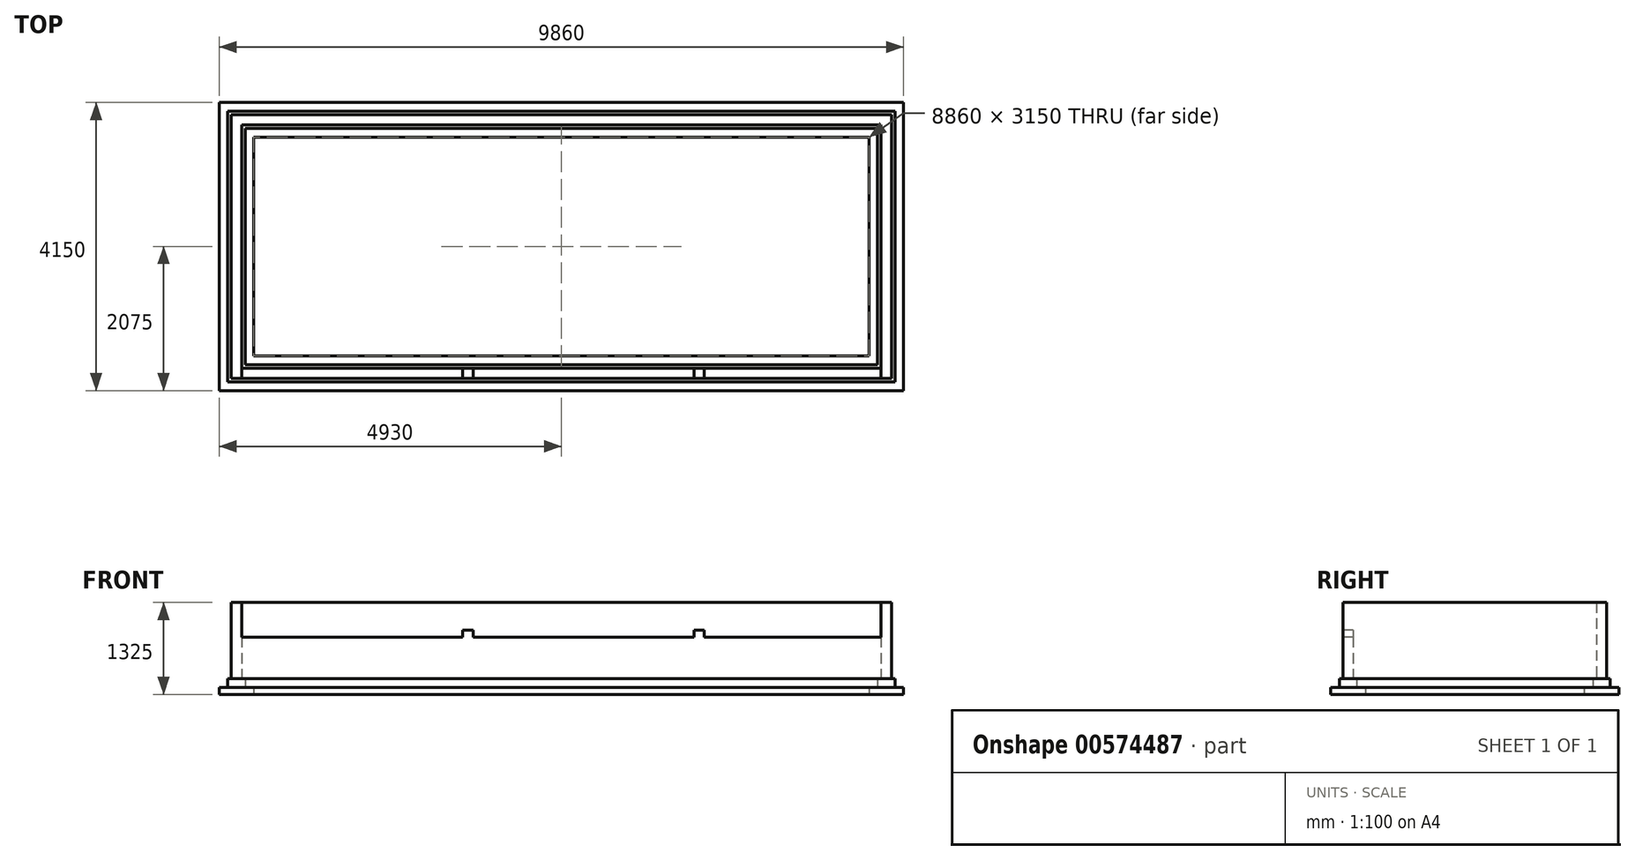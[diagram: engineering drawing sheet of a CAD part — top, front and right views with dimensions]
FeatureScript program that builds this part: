
annotation { "Feature Type Name" : "Feature", "Feature Type Description" : "" }
export const myFeature = defineFeature(function(context is Context, id is Id, definition is map)
    precondition{}
    {
        {
            var Q0;
            Q0=qCreatedBy(makeId("Top.planeOp"),FACE);
            var sketch = newSketch(context, id + "F0", { "sketchPlane" : qUnion([Q0])});
            skLineSegment(sketch, "E0", {"start": v(-2720, 0) * mm, "end": v(-3220, 0) * mm});
            skLineSegment(sketch, "E1", {"start": v(-3220, 0) * mm, "end": v(-3220, 4150) * mm});
            skLineSegment(sketch, "E2", {"start": v(-3220, 4150) * mm, "end": v(6640, 4150) * mm});
            skLineSegment(sketch, "E3", {"start": v(6640, 4150) * mm, "end": v(6640, 0) * mm});
            skLineSegment(sketch, "E4", {"start": v(6640, 0) * mm, "end": v(6140, 0) * mm});
            skLineSegment(sketch, "E5", {"start": v(6140, 500) * mm, "end": v(6140, 3650) * mm});
            skLineSegment(sketch, "E6", {"start": v(6140, 3650) * mm, "end": v(-2720, 3650) * mm});
            skLineSegment(sketch, "E7", {"start": v(-2720, 3650) * mm, "end": v(-2720, 500) * mm});
            skLineSegment(sketch, "E8", {"start": v(-2720, 0) * mm, "end": v(6140, 0) * mm});
            skLineSegment(sketch, "E9", {"start": v(-2970, 0) * mm, "end": v(-2970, 3900) * mm, "construction": true});
            skLineSegment(sketch, "E10", {"start": v(-2970, 3900) * mm, "end": v(6390, 3900) * mm, "construction": true});
            skLineSegment(sketch, "E11", {"start": v(6390, 0) * mm, "end": v(6390, 3900) * mm, "construction": true});
            skLineSegment(sketch, "E12", {"start": v(-2720, 500) * mm, "end": v(6140, 500) * mm});
            skLineSegment(sketch, "E13", {"start": v(-2970, 250) * mm, "end": v(6390, 250) * mm, "construction": true});
            skSolve(sketch);
        }
        {
            var Q0;
            Q0=makeQuery(id+"F0.imprint","IMPRINT",FACE,{"disambiguationData":[TD([[makeQuery(id+"F0.imprint","IMPRINT",EDGE,{"derivedFrom":sQuery(id+"F0.wireOp",EDGE,"E0")}),-1.0]])]});
            extrude(context, id + "F1", {"entities" : qUnion([Q0]), "depth" : 100 * mm, "offsetDistance" : 25 * mm});
        }
        {
            var Q0;
            Q0=makeQuery(id+"F1.opExtrude","CAP_FACE",FACE,{"disambiguationData":[OSD([sQuery(id+"F0.wireOp",EDGE,"E0"),sQuery(id+"F0.wireOp",EDGE,"E1"),sQuery(id+"F0.wireOp",EDGE,"E2"),sQuery(id+"F0.wireOp",EDGE,"E3"),sQuery(id+"F0.wireOp",EDGE,"E4"),sQuery(id+"F0.wireOp",EDGE,"E5"),sQuery(id+"F0.wireOp",EDGE,"E6"),sQuery(id+"F0.wireOp",EDGE,"E7")])],"isStart":false});
            var sketch = newSketch(context, id + "F2", { "sketchPlane" : qUnion([Q0])});
            skLineSegment(sketch, "E14", {"start": v(-3095, 125) * mm, "end": v(-3095, 4025) * mm});
            skLineSegment(sketch, "E15", {"start": v(-3095, 4025) * mm, "end": v(6515, 4025) * mm});
            skLineSegment(sketch, "E16", {"start": v(6515, 4025) * mm, "end": v(6515, 125) * mm});
            skLineSegment(sketch, "E17", {"start": v(6265, 375) * mm, "end": v(6265, 3775) * mm});
            skLineSegment(sketch, "E18", {"start": v(6265, 3775) * mm, "end": v(-2845, 3775) * mm});
            skLineSegment(sketch, "E19", {"start": v(-2845, 3775) * mm, "end": v(-2845, 375) * mm});
            skLineSegment(sketch, "E20", {"start": v(-2845, 375) * mm, "end": v(6265, 375) * mm});
            skLineSegment(sketch, "E21", {"start": v(-3095, 125) * mm, "end": v(6515, 125) * mm});
            skPoint(sketch, "E22.orphan", {"position": v(-2845, 0) * mm});
            skPoint(sketch, "E23.orphan", {"position": v(6515, 0) * mm});
            skSolve(sketch);
        }
        {
            var Q0;
            Q0=makeQuery(id+"F2.imprint","IMPRINT",FACE,{"disambiguationData":[TD([[makeQuery(id+"F2.imprint","IMPRINT",EDGE,{"derivedFrom":sQuery(id+"F2.wireOp",EDGE,"E14")}),-1.0]])]});
            extrude(context, id + "F3", {"entities" : qUnion([Q0]), "operationType" : NewBodyOperationType.ADD, "depth" : 100 * mm, "offsetDistance" : 25 * mm});
        }
        {
            var Q0;
            Q0=makeQuery(id+"F3.opExtrude","CAP_FACE",FACE,{"disambiguationData":[OSD([sQuery(id+"F2.wireOp",EDGE,"E14"),sQuery(id+"F2.wireOp",EDGE,"E15"),sQuery(id+"F2.wireOp",EDGE,"E16"),sQuery(id+"F2.wireOp",EDGE,"NphoCxTZ-fXz7-NrUu-ey8z-QnH2uSn7Xx2u"),sQuery(id+"F2.wireOp",EDGE,"E17"),sQuery(id+"F2.wireOp",EDGE,"E18"),sQuery(id+"F2.wireOp",EDGE,"E19"),sQuery(id+"F2.wireOp",EDGE,"ZqT3Uk6X-4e9T-K1ZI-z1TJ-C3bCra6QGol4")])],"isStart":false});
            extrude(context, id + "F4", {"entities" : qUnion([Q0]), "operationType" : NewBodyOperationType.ADD, "depth" : 25 * mm, "offsetDistance" : 25 * mm});
        }
        {
            var Q0;
            Q0=makeQuery(id+"F4.opExtrude","CAP_FACE",FACE,{"disambiguationData":[OSD([sQuery(id+"F2.wireOp",EDGE,"E14"),sQuery(id+"F2.wireOp",EDGE,"E15"),sQuery(id+"F2.wireOp",EDGE,"E16"),sQuery(id+"F2.wireOp",EDGE,"NphoCxTZ-fXz7-NrUu-ey8z-QnH2uSn7Xx2u"),sQuery(id+"F2.wireOp",EDGE,"E17"),sQuery(id+"F2.wireOp",EDGE,"E18"),sQuery(id+"F2.wireOp",EDGE,"E19"),sQuery(id+"F2.wireOp",EDGE,"ZqT3Uk6X-4e9T-K1ZI-z1TJ-C3bCra6QGol4")])],"isStart":false});
            var sketch = newSketch(context, id + "F5", { "sketchPlane" : qUnion([Q0])});
            skLineSegment(sketch, "E24", {"start": v(-3045, 175) * mm, "end": v(-3045, 3975) * mm});
            skLineSegment(sketch, "E25", {"start": v(-3045, 3975) * mm, "end": v(6465, 3975) * mm});
            skLineSegment(sketch, "E26", {"start": v(6465, 3975) * mm, "end": v(6465, 175) * mm});
            skLineSegment(sketch, "E27", {"start": v(6465, 175) * mm, "end": v(6315, 175) * mm});
            skLineSegment(sketch, "E28", {"start": v(6315, 175) * mm, "end": v(6315, 3825) * mm});
            skLineSegment(sketch, "E29", {"start": v(6315, 3825) * mm, "end": v(-2895, 3825) * mm});
            skLineSegment(sketch, "E30", {"start": v(-2895, 3825) * mm, "end": v(-2895, 175) * mm});
            skLineSegment(sketch, "E31", {"start": v(-2895, 175) * mm, "end": v(-3045, 175) * mm});
            skPoint(sketch, "E32.orphan", {"position": v(-2895, 125) * mm});
            skPoint(sketch, "E33.orphan", {"position": v(6465, 125) * mm});
            skSolve(sketch);
        }
        {
            var Q0;
            {var subQ3=sQuery(id+"F5.wireOp",EDGE,"E27");Q0=makeQuery(id+"F5.imprint","IMPRINT",FACE,{"disambiguationData":[TD([[makeQuery(id+"F5.imprint","IMPRINT",EDGE,{"derivedFrom":subQ3}),-1.0]])]});}
            extrude(context, id + "F6", {"entities" : qUnion([Q0]), "operationType" : NewBodyOperationType.ADD, "depth" : 1100 * mm, "offsetDistance" : 25 * mm});
        }
        {
            var Q0;
            Q0=makeQuery(id+"F4.opExtrude","CAP_FACE",FACE,{"disambiguationData":[OSD([sQuery(id+"F2.wireOp",EDGE,"E14"),sQuery(id+"F2.wireOp",EDGE,"E15"),sQuery(id+"F2.wireOp",EDGE,"E16"),sQuery(id+"F2.wireOp",EDGE,"E17"),sQuery(id+"F2.wireOp",EDGE,"E18"),sQuery(id+"F2.wireOp",EDGE,"E19"),sQuery(id+"F2.wireOp",EDGE,"E20"),sQuery(id+"F2.wireOp",EDGE,"E21")])],"isStart":false});
            var sketch = newSketch(context, id + "F7", { "sketchPlane" : qUnion([Q0])});
            skLineSegment(sketch, "E34.bottom", {"start": v(-2895, 175) * mm, "end": v(6315, 175) * mm});
            skLineSegment(sketch, "E34.top", {"start": v(-2895, 325) * mm, "end": v(6315, 325) * mm});
            skLineSegment(sketch, "E34.left", {"start": v(-2895, 175) * mm, "end": v(-2895, 325) * mm});
            skLineSegment(sketch, "E34.right", {"start": v(6315, 175) * mm, "end": v(6315, 325) * mm});
            skSolve(sketch);
        }
        {
            var Q0;
            Q0 = qSketchRegion(id + "F7", true);
            extrude(context, id + "F8", {"entities" : qUnion([Q0]), "operationType" : NewBodyOperationType.ADD, "depth" : 600 * mm, "offsetDistance" : 25 * mm});
        }
        {
            var Q0;
            Q0=makeQuery(id+"F8.opExtrude","CAP_FACE",FACE,{"disambiguationData":[OSD([sQuery(id+"F7.wireOp",EDGE,"E34.bottom"),sQuery(id+"F7.wireOp",EDGE,"E34.top"),sQuery(id+"F7.wireOp",EDGE,"E34.left"),sQuery(id+"F7.wireOp",EDGE,"E34.right")])],"isStart":false});
            var sketch = newSketch(context, id + "F9", { "sketchPlane" : qUnion([Q0])});
            skLineSegment(sketch, "E35.bottom", {"start": v(290, 325) * mm, "end": v(440, 325) * mm});
            skLineSegment(sketch, "E35.top", {"start": v(290, 175) * mm, "end": v(440, 175) * mm});
            skLineSegment(sketch, "E35.left", {"start": v(290, 325) * mm, "end": v(290, 175) * mm});
            skLineSegment(sketch, "E35.right", {"start": v(440, 325) * mm, "end": v(440, 175) * mm});
            skLineSegment(sketch, "E36.bottom", {"start": v(3620, 325) * mm, "end": v(3770, 325) * mm});
            skLineSegment(sketch, "E36.top", {"start": v(3620, 175) * mm, "end": v(3770, 175) * mm});
            skLineSegment(sketch, "E36.left", {"start": v(3620, 325) * mm, "end": v(3620, 175) * mm});
            skLineSegment(sketch, "E36.right", {"start": v(3770, 325) * mm, "end": v(3770, 175) * mm});
            skSolve(sketch);
        }
        {
            var Q0;
            Q0 = qSketchRegion(id + "F9", true);
            extrude(context, id + "F10", {"entities" : qUnion([Q0]), "operationType" : NewBodyOperationType.ADD, "depth" : 100 * mm, "offsetDistance" : 25 * mm});
        }
    });
